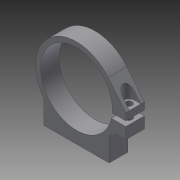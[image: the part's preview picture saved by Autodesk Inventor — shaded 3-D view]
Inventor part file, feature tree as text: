
AUTODESK INVENTOR PART (.ipt)
format: ipt  version: 2014 SP1 (Build 180222100, 222)  size: 134,144 bytes
history: native  units: in
note: dims shown in document units (in); Inventor stores cm internally (conversion verified against a paired STEP export)
features: sketch x5, other x3
ambient origin geometry x8: Origin, YZ Plane, XZ Plane, XY Plane, X Axis, Y Axis, Z Axis, Center Point
bodies: Solid1 (feature_tree)
feature tree (8):
  other  "Motor Mount.ipt"
  other  "Solid1::Motor Mount.ipt"
  other  "TaggingFeature1"
  sketch  "Sketch1"  dims[d0=0.3937in]
  sketch  "Sketch2"  dims[d1=1.65in d9=0.375in d10=0.0in d12=1.061in d13=0.138in d14=0.138in d15=0.375in d16=0.0in d21=0.125in d22=0.138in d23=1.0in d24=0.0in d26=0.4in d27=0.23in d28=0.125in d29=0.0in d30=0.375in d31=0.0in]
  sketch  "Sketch3"
  sketch  "Sketch4"
  sketch  "Sketch5"
